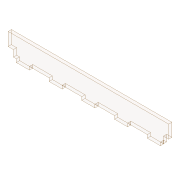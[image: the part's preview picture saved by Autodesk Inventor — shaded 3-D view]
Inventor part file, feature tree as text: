
AUTODESK INVENTOR PART (.ipt)
format: ipt  version: 2020 (Build 240168000, 168)  size: 124,416 bytes
history: native  units: mm
features: extrude x3, sketch x3
ambient origin geometry x8: Origin, YZ Plane, XZ Plane, XY Plane, X Axis, Y Axis, Z Axis, Center Point
bodies: Solid1 (feature_tree)
feature tree (6):
  extrude  "Extrusion1"  Depth=245.0mm
  extrude  "Extrusion2"  Depth=20.0mm
  extrude  "Extrusion3"  Depth=12.5mm
  sketch  "Sketch1"  dims[d0=30.0mm d1=245.0mm]
  sketch  "Sketch2"  dims[d2=5.0mm d3=0.0mm d4=20.0mm]
  sketch  "Sketch3"  dims[d5=5.0mm d6=12.5mm d7=50.0mm d9=50.0mm d10=10.0mm d12=10.0mm d14=5.0mm d15=0.0mm d18=8.0mm d19=10.0mm d20=5.0mm d21=0.0mm]
